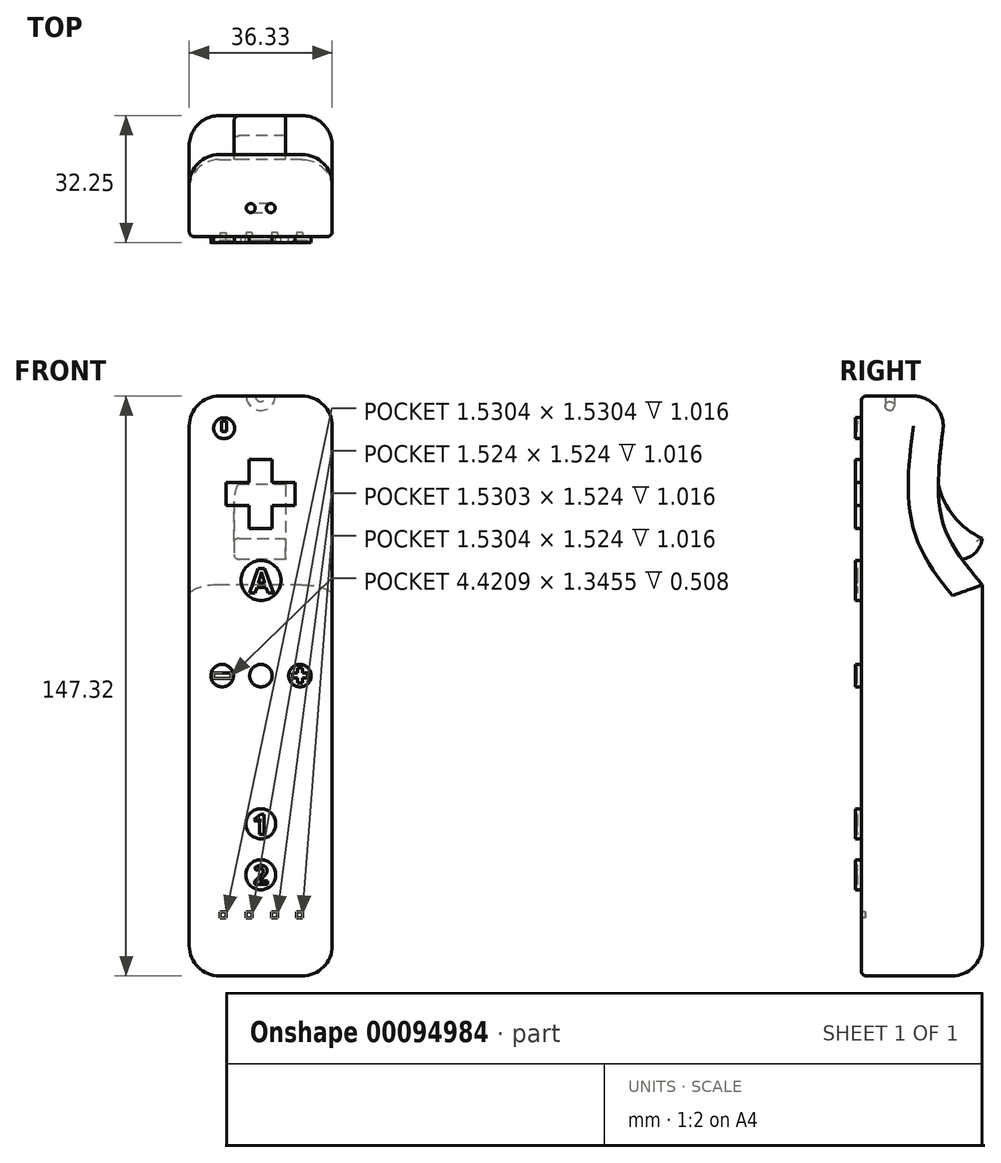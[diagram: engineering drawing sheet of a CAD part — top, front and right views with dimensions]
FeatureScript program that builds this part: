
annotation { "Feature Type Name" : "Feature", "Feature Type Description" : "" }
export const myFeature = defineFeature(function(context is Context, id is Id, definition is map)
    precondition{}
    {
        {
            var Q0;
            Q0=qCreatedBy(makeId("Front.planeOp"),FACE);
            var sketch = newSketch(context, id + "F0", { "sketchPlane" : qUnion([Q0])});
            skLineSegment(sketch, "E0.bottom", {"start": v(16.75, 69.43) * mm, "end": v(53.08, 69.43) * mm});
            skLineSegment(sketch, "E0.top", {"start": v(16.75, -77.89) * mm, "end": v(53.08, -77.89) * mm});
            skLineSegment(sketch, "E0.left", {"start": v(16.75, 69.43) * mm, "end": v(16.75, -77.89) * mm});
            skLineSegment(sketch, "E0.right", {"start": v(53.08, 69.43) * mm, "end": v(53.08, -77.89) * mm});
            skLineSegment(sketch, "E1", {"start": v(16.75, -4.23) * mm, "end": v(53.08, -4.23) * mm, "construction": true});
            skLineSegment(sketch, "E2", {"start": v(16.75, 69.43) * mm, "end": v(16.75, 61.2) * mm, "construction": true});
            skLineSegment(sketch, "E3", {"start": v(34.91, 69.43) * mm, "end": v(34.91, -77.89) * mm, "construction": true});
            skLineSegment(sketch, "E4", {"start": v(16.77, -4.17) * mm, "end": v(53.1, -4.17) * mm, "construction": true});
            skCircle(sketch, "E5", {"center": v(35, 22.59) * mm, "radius": 5.08 * mm});
            skLineSegment(sketch, "E6", {"start": v(31.9, 53.27) * mm, "end": v(37.74, 53.27) * mm});
            skLineSegment(sketch, "E7", {"start": v(37.74, 53.27) * mm, "end": v(37.74, 47.43) * mm});
            skLineSegment(sketch, "E8", {"start": v(37.74, 47.43) * mm, "end": v(43.58, 47.43) * mm});
            skLineSegment(sketch, "E9", {"start": v(43.58, 47.43) * mm, "end": v(43.58, 41.59) * mm});
            skLineSegment(sketch, "E10", {"start": v(43.58, 41.59) * mm, "end": v(37.74, 41.59) * mm});
            skLineSegment(sketch, "E11", {"start": v(37.74, 41.59) * mm, "end": v(37.74, 35.74) * mm});
            skLineSegment(sketch, "E12", {"start": v(37.74, 35.74) * mm, "end": v(31.9, 35.74) * mm});
            skLineSegment(sketch, "E13", {"start": v(31.9, 35.74) * mm, "end": v(31.9, 41.59) * mm});
            skLineSegment(sketch, "E14", {"start": v(31.9, 41.59) * mm, "end": v(26.04, 41.59) * mm});
            skLineSegment(sketch, "E15", {"start": v(26.04, 41.59) * mm, "end": v(26.04, 47.43) * mm});
            skLineSegment(sketch, "E16", {"start": v(26.04, 47.43) * mm, "end": v(31.9, 47.43) * mm});
            skLineSegment(sketch, "E17", {"start": v(31.9, 47.43) * mm, "end": v(31.9, 53.27) * mm});
            skCircle(sketch, "E18", {"center": v(25.62, 61.26) * mm, "radius": 2.66 * mm});
            skPoint(sketch, "E19.startSnap0", {"position": v(34.93, -4.17) * mm});
            skCircle(sketch, "E20", {"center": v(25.11, -1.62) * mm, "radius": 2.86 * mm});
            skCircle(sketch, "E21", {"center": v(34.97, -1.62) * mm, "radius": 2.86 * mm});
            skCircle(sketch, "E22", {"center": v(44.88, -1.62) * mm, "radius": 2.86 * mm});
            skLineSegment(sketch, "E23", {"start": v(34.93, 69.5) * mm, "end": v(34.93, -77.83) * mm, "construction": true});
            skCircle(sketch, "E24", {"center": v(34.93, -52.21) * mm, "radius": 3.81 * mm});
            skCircle(sketch, "E25", {"center": v(34.93, -39.25) * mm, "radius": 3.81 * mm});
            skLineSegment(sketch, "E26.bottom", {"start": v(24.61, -63.16) * mm, "end": v(26.14, -63.16) * mm});
            skLineSegment(sketch, "E26.top", {"start": v(24.61, -61.63) * mm, "end": v(26.14, -61.63) * mm});
            skLineSegment(sketch, "E26.left", {"start": v(24.61, -63.16) * mm, "end": v(24.61, -61.63) * mm});
            skLineSegment(sketch, "E26.right", {"start": v(26.14, -63.16) * mm, "end": v(26.14, -61.63) * mm});
            skLineSegment(sketch, "E27.bottom", {"start": v(32.76, -61.63) * mm, "end": v(31.24, -61.63) * mm});
            skLineSegment(sketch, "E27.top", {"start": v(32.76, -63.16) * mm, "end": v(31.24, -63.16) * mm});
            skLineSegment(sketch, "E27.left", {"start": v(32.76, -61.63) * mm, "end": v(32.76, -63.16) * mm});
            skLineSegment(sketch, "E27.right", {"start": v(31.24, -61.63) * mm, "end": v(31.24, -63.16) * mm});
            skLineSegment(sketch, "E28.bottom", {"start": v(39.14, -61.63) * mm, "end": v(37.6, -61.63) * mm});
            skLineSegment(sketch, "E28.top", {"start": v(39.14, -63.16) * mm, "end": v(37.6, -63.16) * mm});
            skLineSegment(sketch, "E28.left", {"start": v(39.14, -61.63) * mm, "end": v(39.14, -63.16) * mm});
            skLineSegment(sketch, "E28.right", {"start": v(37.6, -61.63) * mm, "end": v(37.6, -63.16) * mm});
            skPoint(sketch, "E29.oppositeSnap0", {"position": v(38.37, -63.16) * mm});
            skLineSegment(sketch, "E29.bottom", {"start": v(45.54, -61.63) * mm, "end": v(44, -61.63) * mm});
            skLineSegment(sketch, "E29.top", {"start": v(45.54, -63.16) * mm, "end": v(44, -63.16) * mm});
            skLineSegment(sketch, "E29.left", {"start": v(45.54, -61.63) * mm, "end": v(45.54, -63.16) * mm});
            skLineSegment(sketch, "E29.right", {"start": v(44, -61.63) * mm, "end": v(44, -63.16) * mm});
            skSolve(sketch);
        }
        {
            var Q0;
            Q0=makeQuery(id+"F0.imprint","IMPRINT",FACE,{"disambiguationData":[TD([[makeQuery(id+"F0.imprint","IMPRINT",EDGE,{"derivedFrom":sQuery(id+"F0.wireOp",EDGE,"E0.bottom")}),-1.0]])]});
            var sketch = newSketch(context, id + "F1", { "sketchPlane" : qUnion([Q0])});
            skLineSegment(sketch, "E30.bottom", {"start": v(16.75, -77.89) * mm, "end": v(53.08, -77.89) * mm});
            skLineSegment(sketch, "E30.top", {"start": v(16.75, 69.43) * mm, "end": v(53.08, 69.43) * mm});
            skLineSegment(sketch, "E30.left", {"start": v(16.75, -77.89) * mm, "end": v(16.75, 69.43) * mm});
            skLineSegment(sketch, "E30.right", {"start": v(53.08, -77.89) * mm, "end": v(53.08, 69.43) * mm});
            skSolve(sketch);
        }
        {
            var Q0;
            Q0 = qSketchRegion(id + "F1", true);
            extrude(context, id + "F2", {"entities" : qUnion([Q0]), "oppositeDirection" : true, "depth" : 30.73 * mm});
        }
        {
            var Q0;
            Q0=makeQuery(id+"F2.opExtrude","SWEPT_FACE",FACE,{"disambiguationData":[OSD([sQuery(id+"F1.wireOp",EDGE,"E30.left")])]});
            var sketch = newSketch(context, id + "F3", { "sketchPlane" : qUnion([Q0])});
            skLineSegment(sketch, "E31", {"start": v(-15.37, 69.43) * mm, "end": v(-15.37, -77.89) * mm, "construction": true});
            skFitSpline(sketch, "E32.MirrorCS", {"points": [v(-21.98, 69.43) * mm, v(-19.68, 43.14) * mm, v(-23.3, 31.48) * mm, v(-30.73, 21.46) * mm], "startDerivative": vector(10.07, -68.56) * mm, "endDerivative": vector(-28.1, -34.04) * mm});
            skSolve(sketch);
        }
        {
            var Q0;
            {var subQ0=sQuery(id+"F3.wireOp",EDGE,"E32.MirrorCS");Q0=makeQuery(id+"F3.imprint","IMPRINT",FACE,{"disambiguationData":[TD([[makeQuery(id+"F3.imprint","IMPRINT",EDGE,{"derivedFrom":subQ0}),-1.0]])]});}
            extrude(context, id + "F4", {"entities" : qUnion([Q0]), "operationType" : NewBodyOperationType.REMOVE, "oppositeDirection" : true, "depth" : 37.6 * mm});
        }
        {
            var Q0;
            Q0=makeQuery(id+"F2.opExtrude","SWEPT_EDGE",EDGE,{"disambiguationData":[OSD([sQuery(id+"F1.wireOp",EDGE,"E30.bottom"),sQuery(id+"F1.wireOp",EDGE,"E30.left")])]});
            var Q1;
            Q1=makeQuery(id+"F2.opExtrude","SWEPT_EDGE",EDGE,{"disambiguationData":[OSD([sQuery(id+"F1.wireOp",EDGE,"E30.bottom"),sQuery(id+"F1.wireOp",EDGE,"E30.right")])]});
            var Q2;
            Q2=makeQuery(id+"F2.opExtrude","SWEPT_EDGE",EDGE,{"disambiguationData":[OSD([sQuery(id+"F1.wireOp",EDGE,"E30.top"),sQuery(id+"F1.wireOp",EDGE,"E30.right")])]});
            var Q3;
            Q3=makeQuery(id+"F2.opExtrude","SWEPT_EDGE",EDGE,{"disambiguationData":[OSD([sQuery(id+"F1.wireOp",EDGE,"E30.top"),sQuery(id+"F1.wireOp",EDGE,"E30.left")])]});
            fillet(context, id + "F5", {"entities" : qUnion([Q0, Q1, Q2, Q3]), "radius" : 7.62 * mm, "tangentPropagation" : true, "allowEdgeOverflow" : false});
        }
        {
            var Q0;
            Q0=makeQuery(id+"F2.opExtrude","CAP_EDGE",EDGE,{"disambiguationData":[OSD([sQuery(id+"F1.wireOp",EDGE,"E30.left")])],"isStart":false});
            var Q1;
            Q1=makeQuery(id+"F4.boolean.opBoolean","INTERSECT",EDGE,{"derivedFrom":[makeQuery(id+"F2.opExtrude","SWEPT_FACE",FACE,{"disambiguationData":[OSD([sQuery(id+"F1.wireOp",EDGE,"E30.right")])]}),makeQuery(id+"F4.opExtrude","SWEPT_FACE",FACE,{"disambiguationData":[OSD([sQuery(id+"F3.wireOp",EDGE,"E32.MirrorCS")])]})]});
            var Q2;
            Q2=makeQuery(id+"F4.boolean.opBoolean","COPY",EDGE,{"derivedFrom":makeQuery(id+"F4.opExtrude","SWEPT_EDGE",EDGE,{"disambiguationData":[OSD([sQuery(id+"F1.wireOp",EDGE,"E30.left"),sQuery(id+"F3.wireOp",EDGE,"E32.MirrorCS")])]})});
            fillet(context, id + "F6", {"entities" : qUnion([Q0, Q1, Q2]), "radius" : 7.62 * mm, "tangentPropagation" : true, "allowEdgeOverflow" : false});
        }
        {
            var Q0;
            Q0=makeQuery(id+"F2.opExtrude","CAP_FACE",FACE,{"disambiguationData":[OSD([sQuery(id+"F1.wireOp",EDGE,"E30.bottom"),sQuery(id+"F1.wireOp",EDGE,"E30.top"),sQuery(id+"F1.wireOp",EDGE,"E30.left"),sQuery(id+"F1.wireOp",EDGE,"E30.right")])],"isStart":false});
            var sketch = newSketch(context, id + "F7", { "sketchPlane" : qUnion([Q0])});
            skLineSegment(sketch, "E33", {"start": v(-40.46, 46.91) * mm, "end": v(-29, 46.91) * mm});
            skLineSegment(sketch, "E34", {"start": v(-40.04, 27.96) * mm, "end": v(-29.37, 27.96) * mm});
            skLineSegment(sketch, "E35", {"start": v(-29.37, 27.96) * mm, "end": v(-28.13, 27.96) * mm});
            skLineSegment(sketch, "E36", {"start": v(-40.04, 27.96) * mm, "end": v(-41.28, 27.96) * mm});
            skLineSegment(sketch, "E37", {"start": v(-41.28, 27.96) * mm, "end": v(-41.28, 47.56) * mm});
            skLineSegment(sketch, "E38", {"start": v(-28.13, 27.96) * mm, "end": v(-28.13, 47.72) * mm});
            skLineSegment(sketch, "E39", {"start": v(-40.46, 46.91) * mm, "end": v(-41.28, 46.91) * mm});
            skLineSegment(sketch, "E40", {"start": v(-29, 46.91) * mm, "end": v(-28.13, 46.91) * mm});
            skSolve(sketch);
        }
        {
            var Q0;
            {var subQ4=sQuery(id+"F7.wireOp",EDGE,"E33");Q0=makeQuery(id+"F7.imprint","IMPRINT",FACE,{"disambiguationData":[TD([[makeQuery(id+"F7.imprint","IMPRINT",EDGE,{"derivedFrom":subQ4}),-1.0]])]});}
            var Q1;
            {var subQ0=sQuery(id+"F7.wireOp",EDGE,"K0iS9Brb-cHPL-CKC8-FlRW-324IReGAGtPr");Q1=makeQuery(id+"F7.imprint","IMPRINT",FACE,{"disambiguationData":[TD([[makeQuery(id+"F7.imprint","IMPRINT",EDGE,{"derivedFrom":subQ0}),-1.0]])]});}
            var Q2;
            {var subQ0=sQuery(id+"F7.wireOp",EDGE,"2nC9m2D6-XAsA-QYTj-u19b-e1dphaC4PzCX");Q2=makeQuery(id+"F7.imprint","IMPRINT",FACE,{"disambiguationData":[TD([[makeQuery(id+"F7.imprint","IMPRINT",EDGE,{"derivedFrom":subQ0}),1.0]])]});}
            extrude(context, id + "F8", {"entities" : qUnion([Q0, Q1, Q2]), "operationType" : NewBodyOperationType.ADD, "oppositeDirection" : true, "depth" : 12.7 * mm});
        }
        {
            var Q0;
            Q0=makeQuery(id+"F8.opExtrude","SWEPT_FACE",FACE,{"disambiguationData":[OSD([sQuery(id+"F7.wireOp",EDGE,"E37")])]});
            var sketch = newSketch(context, id + "F9", { "sketchPlane" : qUnion([Q0])});
            skArc(sketch, "E41", {"start": v(19.57, 46.91) * mm, "mid": v(23.59, 38.8) * mm, "end": v(30.73, 33.22) * mm});
            skArc(sketch, "E42", {"start": v(25.6, 27.96) * mm, "mid": v(29.07, 29.72) * mm, "end": v(30.73, 33.22) * mm});
            skSolve(sketch);
        }
        {
            var Q0;
            {var subQ0=sQuery(id+"F9.wireOp",EDGE,"E41");Q0=makeQuery(id+"F9.imprint","IMPRINT",FACE,{"disambiguationData":[TD([[makeQuery(id+"F9.imprint","IMPRINT",EDGE,{"derivedFrom":subQ0}),1.0]])]});}
            var Q1;
            {var subQ0=sQuery(id+"F9.wireOp",EDGE,"oilb41jp-Mc1F-x8EU-rBpX-l4kon2PeC7sV");Q1=makeQuery(id+"F9.imprint","IMPRINT",FACE,{"disambiguationData":[TD([[makeQuery(id+"F9.imprint","IMPRINT",EDGE,{"derivedFrom":subQ0}),-1.0]])]});}
            var Q2;
            {var subQ0=sQuery(id+"F9.wireOp",EDGE,"E42");Q2=makeQuery(id+"F9.imprint","IMPRINT",FACE,{"disambiguationData":[TD([[makeQuery(id+"F9.imprint","IMPRINT",EDGE,{"derivedFrom":subQ0}),-1.0]])]});}
            extrude(context, id + "F10", {"entities" : qUnion([Q0, Q1, Q2]), "operationType" : NewBodyOperationType.REMOVE, "oppositeDirection" : true, "depth" : 15.24 * mm});
        }
        {
            var Q0;
            Q0=makeQuery(id+"F0.imprint","IMPRINT",FACE,{"disambiguationData":[TD([[makeQuery(id+"F0.imprint","IMPRINT",EDGE,{"derivedFrom":sQuery(id+"F0.wireOp",EDGE,"E6")}),-1.0]])]});
            var Q1;
            Q1=makeQuery(id+"F0.imprint","IMPRINT",FACE,{"disambiguationData":[TD([[makeQuery(id+"F0.imprint","IMPRINT",EDGE,{"derivedFrom":sQuery(id+"F0.wireOp",EDGE,"E18")}),1.0]])]});
            var Q2;
            Q2=makeQuery(id+"F0.imprint","IMPRINT",FACE,{"disambiguationData":[TD([[makeQuery(id+"F0.imprint","IMPRINT",EDGE,{"derivedFrom":sQuery(id+"F0.wireOp",EDGE,"E5")}),1.0]])]});
            var Q3;
            Q3=makeQuery(id+"F0.imprint","IMPRINT",FACE,{"disambiguationData":[TD([[makeQuery(id+"F0.imprint","IMPRINT",EDGE,{"derivedFrom":sQuery(id+"F0.wireOp",EDGE,"E21")}),1.0]])]});
            var Q4;
            Q4=makeQuery(id+"F0.imprint","IMPRINT",FACE,{"disambiguationData":[TD([[makeQuery(id+"F0.imprint","IMPRINT",EDGE,{"derivedFrom":sQuery(id+"F0.wireOp",EDGE,"E20")}),1.0]])]});
            var Q5;
            Q5=makeQuery(id+"F0.imprint","IMPRINT",FACE,{"disambiguationData":[TD([[makeQuery(id+"F0.imprint","IMPRINT",EDGE,{"derivedFrom":sQuery(id+"F0.wireOp",EDGE,"E22")}),1.0]])]});
            var Q6;
            Q6=makeQuery(id+"F0.imprint","IMPRINT",FACE,{"disambiguationData":[TD([[makeQuery(id+"F0.imprint","IMPRINT",EDGE,{"derivedFrom":sQuery(id+"F0.wireOp",EDGE,"E25")}),1.0]])]});
            var Q7;
            Q7=makeQuery(id+"F0.imprint","IMPRINT",FACE,{"disambiguationData":[TD([[makeQuery(id+"F0.imprint","IMPRINT",EDGE,{"derivedFrom":sQuery(id+"F0.wireOp",EDGE,"E24")}),1.0]])]});
            extrude(context, id + "F11", {"entities" : qUnion([Q0, Q1, Q2, Q3, Q4, Q5, Q6, Q7]), "operationType" : NewBodyOperationType.ADD, "depth" : 1.52 * mm});
        }
        {
            var Q0;
            Q0=makeQuery(id+"F0.imprint","IMPRINT",FACE,{"disambiguationData":[TD([[makeQuery(id+"F0.imprint","IMPRINT",EDGE,{"derivedFrom":sQuery(id+"F0.wireOp",EDGE,"E29.bottom")}),1.0]])]});
            var Q1;
            Q1=makeQuery(id+"F0.imprint","IMPRINT",FACE,{"disambiguationData":[TD([[makeQuery(id+"F0.imprint","IMPRINT",EDGE,{"derivedFrom":sQuery(id+"F0.wireOp",EDGE,"E28.bottom")}),1.0]])]});
            var Q2;
            Q2=makeQuery(id+"F0.imprint","IMPRINT",FACE,{"disambiguationData":[TD([[makeQuery(id+"F0.imprint","IMPRINT",EDGE,{"derivedFrom":sQuery(id+"F0.wireOp",EDGE,"E27.bottom")}),1.0]])]});
            var Q3;
            Q3=makeQuery(id+"F0.imprint","IMPRINT",FACE,{"disambiguationData":[TD([[makeQuery(id+"F0.imprint","IMPRINT",EDGE,{"derivedFrom":sQuery(id+"F0.wireOp",EDGE,"E26.bottom")}),1.0]])]});
            extrude(context, id + "F12", {"entities" : qUnion([Q0, Q1, Q2, Q3]), "operationType" : NewBodyOperationType.REMOVE, "oppositeDirection" : true, "depth" : 1.02 * mm});
        }
        {
            var Q0;
            Q0=makeQuery(id+"F2.opExtrude","CAP_EDGE",EDGE,{"disambiguationData":[OSD([sQuery(id+"F1.wireOp",EDGE,"E30.left")])],"isStart":true});
            fillet(context, id + "F13", {"entities" : qUnion([Q0]), "radius" : 1.27 * mm, "tangentPropagation" : true, "allowEdgeOverflow" : false});
        }
        {
            var Q0;
            {var subQ0=sQuery(id+"F9.wireOp",EDGE,"E42");var subQ1=sQuery(id+"F7.wireOp",EDGE,"E37");var subQ2=sQuery(id+"F9.wireOp",EDGE,"E41");Q0=makeQuery(id+"F10.boolean.opBoolean","TWEAK_EDGE",EDGE,{"derivedFrom":[makeQuery(id+"F10.opExtrude","SWEPT_EDGE",EDGE,{"disambiguationData":[OSD([subQ1,subQ2,subQ0]),ownerDisambiguation([makeQuery(id+"F10.opExtrude","SWEPT_BODY",BODY,{"disambiguationData":[OSD([subQ1,sQuery(id+"F7.wireOp",EDGE,"E39"),subQ2])]})])]}),makeQuery(id+"F10.opExtrude","SWEPT_EDGE",EDGE,{"disambiguationData":[OSD([subQ1,subQ2,subQ0]),ownerDisambiguation([makeQuery(id+"F10.opExtrude","SWEPT_BODY",BODY,{"disambiguationData":[OSD([sQuery(id+"F7.wireOp",EDGE,"E36"),subQ1,subQ0])]})])]})]});}
            var Q1;
            Q1=makeQuery(id+"F10.boolean.opBoolean","COPY",EDGE,{"derivedFrom":makeQuery(id+"F10.opExtrude","CAP_EDGE",EDGE,{"disambiguationData":[OSD([sQuery(id+"F9.wireOp",EDGE,"E41")])],"isStart":true})});
            var Q2;
            Q2=makeQuery(id+"F10.boolean.opBoolean","INTERSECT",EDGE,{"derivedFrom":[makeQuery(id+"F8.opExtrude","SWEPT_FACE",FACE,{"disambiguationData":[OSD([sQuery(id+"F7.wireOp",EDGE,"E38")])]}),makeQuery(id+"F10.opExtrude","SWEPT_FACE",FACE,{"disambiguationData":[OSD([sQuery(id+"F9.wireOp",EDGE,"E41")])]})]});
            var Q3;
            Q3=makeQuery(id+"F10.boolean.opBoolean","COPY",EDGE,{"derivedFrom":makeQuery(id+"F10.opExtrude","CAP_EDGE",EDGE,{"disambiguationData":[OSD([sQuery(id+"F9.wireOp",EDGE,"E42")])],"isStart":true})});
            var Q4;
            Q4=makeQuery(id+"F10.boolean.opBoolean","INTERSECT",EDGE,{"derivedFrom":[makeQuery(id+"F8.opExtrude","SWEPT_FACE",FACE,{"disambiguationData":[OSD([sQuery(id+"F7.wireOp",EDGE,"E38")])]}),makeQuery(id+"F10.opExtrude","SWEPT_FACE",FACE,{"disambiguationData":[OSD([sQuery(id+"F9.wireOp",EDGE,"E42")])]})]});
            fillet(context, id + "F14", {"entities" : qUnion([Q0, Q1, Q2, Q3, Q4]), "radius" : 1.27 * mm, "tangentPropagation" : true, "allowEdgeOverflow" : false});
        }
        {
            var Q0;
            Q0=makeQuery(id+"F2.opExtrude","SWEPT_FACE",FACE,{"disambiguationData":[OSD([sQuery(id+"F1.wireOp",EDGE,"E30.top")])]});
            var sketch = newSketch(context, id + "F15", { "sketchPlane" : qUnion([Q0])});
            skLineSegment(sketch, "E43", {"start": v(34.91, 13.2) * mm, "end": v(34.91, 1.27) * mm});
            skLineSegment(sketch, "E44", {"start": v(24.37, 7.24) * mm, "end": v(45.46, 7.24) * mm, "construction": true});
            skCircle(sketch, "E45", {"center": v(32.37, 7.24) * mm, "radius": 1.14 * mm});
            skCircle(sketch, "E46", {"center": v(37.45, 7.24) * mm, "radius": 1.14 * mm});
            skLineSegment(sketch, "E47", {"start": v(37.45, 7.24) * mm, "end": v(32.37, 7.24) * mm, "construction": true});
            skSolve(sketch);
        }
        {
            var Q0;
            Q0=makeQuery(id+"F15.imprint","IMPRINT",FACE,{"disambiguationData":[TD([[makeQuery(id+"F15.imprint","IMPRINT",EDGE,{"derivedFrom":sQuery(id+"F15.wireOp",EDGE,"E46")}),1.0]])]});
            var Q1;
            Q1=sQuery(id+"F15.wireOp",EDGE,"E43");
            revolve(context, id + "F16", {"operationType" : NewBodyOperationType.REMOVE, "entities" : qUnion([Q0]), "axis" : qUnion([Q1]), "revolveType" : RevolveType.ONE_DIRECTION, "oppositeDirection" : true, "angle" : 180 * degree});
        }
        {
            var Q0;
            Q0=makeQuery(id+"F11.opExtrude","CAP_FACE",FACE,{"disambiguationData":[OSD([sQuery(id+"F0.wireOp",EDGE,"E5")])],"isStart":false});
            var sketch = newSketch(context, id + "F17", { "sketchPlane" : qUnion([Q0])});
            skText(sketch, "E48", { "text": "A", "fontName": "OpenSans-Bold.ttf"});
            skLineSegment(sketch, "E49.bottom", {"start": v(27.35, -2.32) * mm, "end": v(22.92, -2.32) * mm});
            skLineSegment(sketch, "E49.top", {"start": v(27.35, -0.98) * mm, "end": v(22.92, -0.98) * mm});
            skLineSegment(sketch, "E49.left", {"start": v(27.35, -2.32) * mm, "end": v(27.35, -0.98) * mm});
            skLineSegment(sketch, "E49.right", {"start": v(22.92, -2.32) * mm, "end": v(22.92, -0.98) * mm});
            skPoint(sketch, "E49.middle", {"position": v(25.13, -1.65) * mm});
            skLineSegment(sketch, "E50.bottom", {"start": v(45.51, -3.48) * mm, "end": v(44.24, -3.48) * mm});
            skLineSegment(sketch, "E50.top", {"start": v(45.51, 0.33) * mm, "end": v(44.24, 0.33) * mm});
            skLineSegment(sketch, "E50.left", {"start": v(45.51, -3.48) * mm, "end": v(45.51, -2.21) * mm});
            skLineSegment(sketch, "E50.right", {"start": v(44.24, -3.48) * mm, "end": v(44.24, -2.21) * mm});
            skPoint(sketch, "E50.middle", {"position": v(44.88, -1.57) * mm});
            skLineSegment(sketch, "E51.bottom", {"start": v(46.78, -2.21) * mm, "end": v(45.51, -2.21) * mm});
            skLineSegment(sketch, "E51.top", {"start": v(46.78, -0.93) * mm, "end": v(45.51, -0.93) * mm});
            skLineSegment(sketch, "E51.left", {"start": v(46.78, -2.21) * mm, "end": v(46.78, -0.93) * mm});
            skLineSegment(sketch, "E51.right", {"start": v(42.97, -2.21) * mm, "end": v(42.97, -0.93) * mm});
            skLineSegment(sketch, "E52.trimOffspring", {"start": v(44.24, -0.93) * mm, "end": v(42.97, -0.93) * mm});
            skLineSegment(sketch, "E53.trimOffspring", {"start": v(44.24, -0.93) * mm, "end": v(44.24, 0.33) * mm});
            skLineSegment(sketch, "E54.trimOffspring", {"start": v(45.51, -0.93) * mm, "end": v(45.51, 0.33) * mm});
            skLineSegment(sketch, "E55.trimOffspring", {"start": v(44.24, -2.21) * mm, "end": v(42.97, -2.21) * mm});
            skText(sketch, "E56", { "text": "1", "fontName": "OpenSans-Bold.ttf"});
            skText(sketch, "E57", { "text": "2\n", "fontName": "OpenSans-Bold.ttf"});
            skLineSegment(sketch, "E58.bottom", {"start": v(26.28, 60.43) * mm, "end": v(25, 60.43) * mm});
            skLineSegment(sketch, "E58.left", {"start": v(26.28, 60.43) * mm, "end": v(26.28, 62.34) * mm});
            skLineSegment(sketch, "E58.right", {"start": v(25, 60.43) * mm, "end": v(25, 62.34) * mm});
            skPoint(sketch, "E58.middle", {"position": v(25.64, 61.38) * mm});
            skArc(sketch, "E59", {"start": v(27.16, 61.38) * mm, "mid": v(25.64, 59.86) * mm, "end": v(24.12, 61.38) * mm});
            skArc(sketch, "E60", {"start": v(27.16, 63) * mm, "mid": v(25.64, 59.16) * mm, "end": v(24.12, 63) * mm});
            skArc(sketch, "E61", {"start": v(27.16, 61.38) * mm, "mid": v(25.14, 59.95) * mm, "end": v(24.46, 62.34) * mm});
            skArc(sketch, "E62", {"start": v(27.16, 61.38) * mm, "mid": v(27.08, 61.9) * mm, "end": v(26.82, 62.34) * mm});
            skLineSegment(sketch, "E63", {"start": v(24.46, 62.34) * mm, "end": v(24.12, 63) * mm});
            skLineSegment(sketch, "E64", {"start": v(27.16, 63) * mm, "end": v(26.82, 62.34) * mm});
            skLineSegment(sketch, "E65", {"start": v(25, 62.34) * mm, "end": v(25, 63.1) * mm});
            skLineSegment(sketch, "E66", {"start": v(25, 63.1) * mm, "end": v(26.27, 63.1) * mm});
            skLineSegment(sketch, "E67", {"start": v(26.27, 63.1) * mm, "end": v(26.28, 62.34) * mm});
            const initialGuessF17  = {"E48": [0.03207, 0.01935, 1, 0, 0.00635], "E56": [0.03281, -0.0419, 1, 0, 0.00513], "E57": [0.0331, -0.05461, 1, 0, 0.00476]};
            skSetInitialGuess(sketch, initialGuessF17);
            skSolve(sketch);
        }
        {
            var Q0;
            Q0=makeQuery(id+"F17.imprint","IMPRINT",FACE,{"disambiguationData":[TD([[makeQuery(id+"F17.imprint","IMPRINT",EDGE,{"derivedFrom":sQuery(id+"F17.wireOp",EDGE,"E60")}),-1.0]])]});
            var Q1;
            Q1=makeQuery(id+"F17.imprint","IMPRINT",FACE,{"disambiguationData":[TD([[makeQuery(id+"F17.imprint","IMPRINT",EDGE,{"derivedFrom":sQuery(id+"F17.wireOp",EDGE,"E56.sketch_text.stroke-0")}),-1.0]])]});
            var Q2;
            Q2=makeQuery(id+"F17.imprint","IMPRINT",FACE,{"disambiguationData":[TD([[makeQuery(id+"F17.imprint","IMPRINT",EDGE,{"derivedFrom":sQuery(id+"F17.wireOp",EDGE,"E57.sketch_text.stroke-0")}),-1.0]])]});
            var Q3;
            Q3=makeQuery(id+"F17.imprint","IMPRINT",FACE,{"disambiguationData":[TD([[makeQuery(id+"F17.imprint","IMPRINT",EDGE,{"derivedFrom":sQuery(id+"F17.wireOp",EDGE,"E49.bottom")}),-1.0]])]});
            var Q4;
            Q4=makeQuery(id+"F17.imprint","IMPRINT",FACE,{"disambiguationData":[TD([[makeQuery(id+"F17.imprint","IMPRINT",EDGE,{"derivedFrom":sQuery(id+"F17.wireOp",EDGE,"E50.bottom")}),-1.0]])]});
            var Q5;
            Q5=makeQuery(id+"F17.imprint","IMPRINT",FACE,{"disambiguationData":[TD([[makeQuery(id+"F17.imprint","IMPRINT",EDGE,{"derivedFrom":sQuery(id+"F17.wireOp",EDGE,"E58.bottom")}),-1.0]])]});
            extrude(context, id + "F18", {"entities" : qUnion([Q0, Q1, Q2, Q3, Q4, Q5]), "operationType" : NewBodyOperationType.REMOVE, "oppositeDirection" : true, "depth" : 0.5 * mm});
        }
        {
            var Q0;
            Q0=makeQuery(id+"F17.imprint","IMPRINT",FACE,{"disambiguationData":[TD([[makeQuery(id+"F17.imprint","IMPRINT",EDGE,{"derivedFrom":sQuery(id+"F17.wireOp",EDGE,"E48.sketch_text.stroke-0")}),-1.0]])]});
            extrude(context, id + "F19", {"entities" : qUnion([Q0]), "operationType" : NewBodyOperationType.REMOVE, "oppositeDirection" : true, "depth" : 0.5 * mm});
        }
    });
